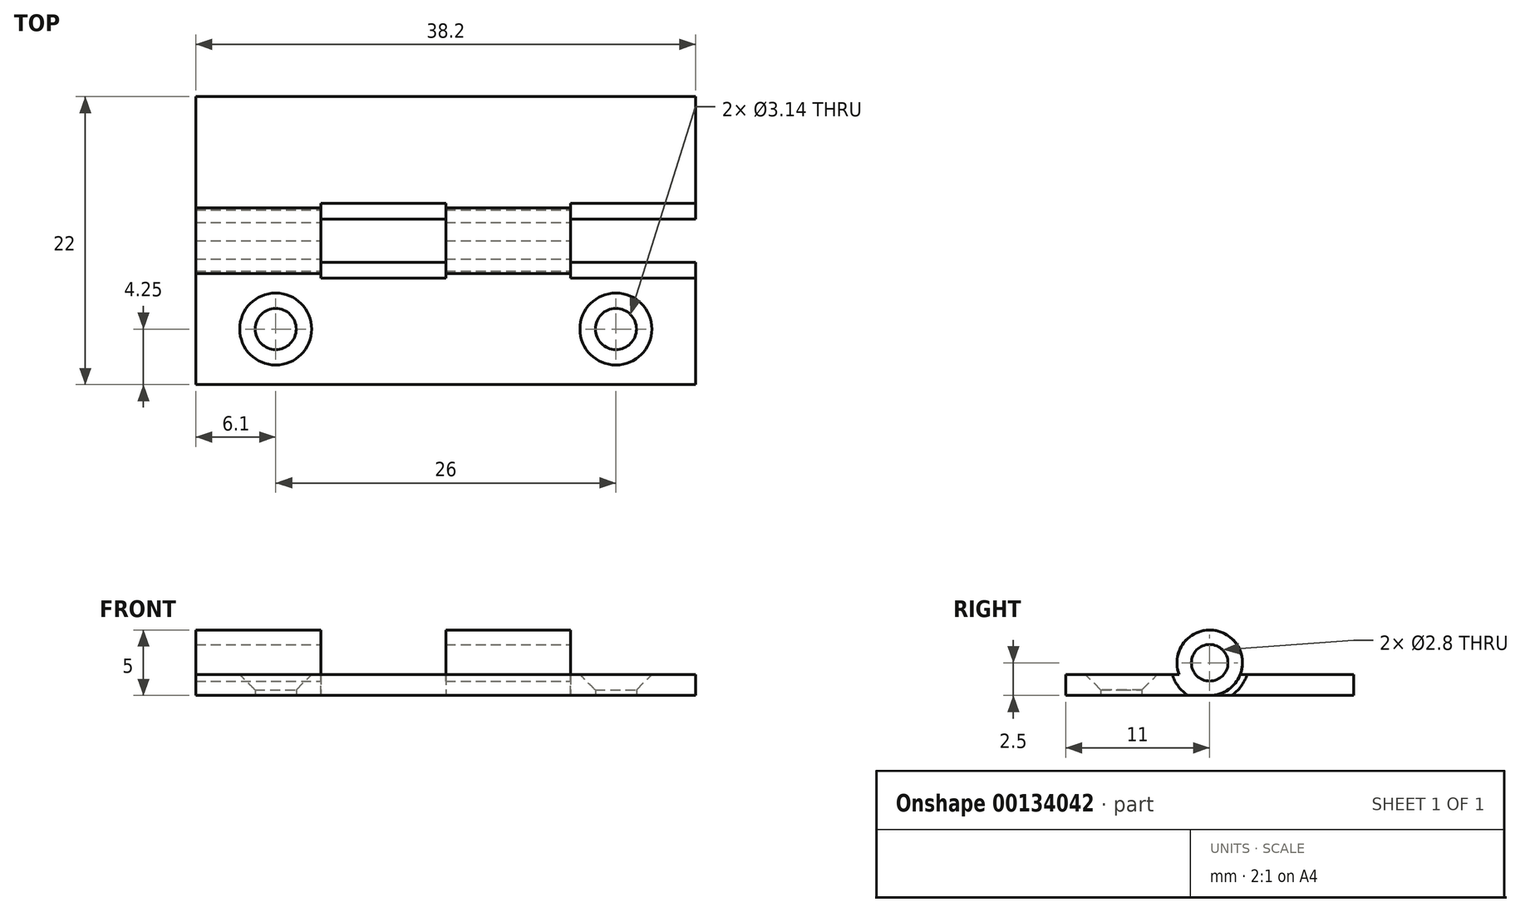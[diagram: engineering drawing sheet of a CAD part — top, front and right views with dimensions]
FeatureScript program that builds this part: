
annotation { "Feature Type Name" : "Feature", "Feature Type Description" : "" }
export const myFeature = defineFeature(function(context is Context, id is Id, definition is map)
    precondition{}
    {
        {
            var Q0;
            Q0=qCreatedBy(makeId("Right.planeOp"),FACE);
            var sketch = newSketch(context, id + "F0", { "sketchPlane" : qUnion([Q0])});
            skCircle(sketch, "E0", {"center": v(0, 0) * mm, "radius": 2.5 * mm});
            skLineSegment(sketch, "E1", {"start": v(0, -2.5) * mm, "end": v(11, -2.5) * mm});
            skLineSegment(sketch, "E2", {"start": v(11, -2.5) * mm, "end": v(11, -0.9) * mm});
            skLineSegment(sketch, "E3", {"start": v(11, -0.9) * mm, "end": v(2.33, -0.9) * mm});
            skLineSegment(sketch, "E4", {"start": v(0, -2.5) * mm, "end": v(0, 0) * mm, "construction": true});
            skLineSegment(sketch, "E5.MirrorCS", {"start": v(-11, -2.5) * mm, "end": v(-11, -0.9) * mm});
            skLineSegment(sketch, "E6.MirrorCS", {"start": v(-11, -0.9) * mm, "end": v(-2.33, -0.9) * mm});
            skLineSegment(sketch, "E7.MirrorCS", {"start": v(0, -2.5) * mm, "end": v(-11, -2.5) * mm});
            skCircle(sketch, "E8", {"center": v(0, 0) * mm, "radius": 1.4 * mm});
            skSolve(sketch);
        }
        {
            var Q0;
            Q0=makeQuery(id+"F0.imprint","IMPRINT",FACE,{"disambiguationData":[TD([[makeQuery(id+"F0.imprint","IMPRINT",EDGE,{"derivedFrom":sQuery(id+"F0.wireOp",EDGE,"E8")}),1.0]])]});
            extrude(context, id + "F1", {"entities" : qUnion([Q0]), "oppositeDirection" : true, "depth" : 38.2 * mm});
        }
        {
            var Q0;
            Q0=makeQuery(id+"F0.imprint","IMPRINT",FACE,{"disambiguationData":[TD([[makeQuery(id+"F0.imprint","IMPRINT",EDGE,{"derivedFrom":sQuery(id+"F0.wireOp",EDGE,"E5.MirrorCS")}),-1.0]])]});
            var Q1;
            Q1=makeQuery(id+"F0.imprint","IMPRINT",FACE,{"disambiguationData":[TD([[makeQuery(id+"F0.imprint","IMPRINT",EDGE,{"derivedFrom":sQuery(id+"F0.wireOp",EDGE,"E8")}),-1.0]])]});
            var Q2;
            Q2=makeQuery(id+"F1.opExtrude","CAP_FACE",FACE,{"disambiguationData":[OSD([sQuery(id+"F0.wireOp",EDGE,"E8")])],"isStart":false});
            extrude(context, id + "F2", {"entities" : qUnion([Q0, Q1]), "endBound" : BoundingType.UP_TO_SURFACE, "oppositeDirection" : true, "endBoundEntityFace" : qUnion([Q2]), "depth" : 38.2 * mm});
        }
        {
            var Q0;
            {var subQ0=sQuery(id+"F0.wireOp",EDGE,"E1");Q0=makeQuery(id+"F0.imprint","IMPRINT",FACE,{"disambiguationData":[TD([[makeQuery(id+"F0.imprint","IMPRINT",EDGE,{"derivedFrom":subQ0}),1.0]])]});}
            var Q1;
            Q1=makeQuery(id+"F0.imprint","IMPRINT",FACE,{"disambiguationData":[TD([[makeQuery(id+"F0.imprint","IMPRINT",EDGE,{"derivedFrom":sQuery(id+"F0.wireOp",EDGE,"E8")}),-1.0]])]});
            var Q2;
            Q2=makeQuery(id+"F1.opExtrude","CAP_FACE",FACE,{"disambiguationData":[OSD([sQuery(id+"F0.wireOp",EDGE,"E8")])],"isStart":false});
            extrude(context, id + "F3", {"entities" : qUnion([Q0, Q1]), "endBound" : BoundingType.UP_TO_SURFACE, "oppositeDirection" : true, "endBoundEntityFace" : qUnion([Q2]), "depth" : 25 * mm});
        }
        {
            var Q0;
            Q0=makeQuery(id+"F2.opExtrude","SWEPT_FACE",FACE,{"disambiguationData":[OSD([sQuery(id+"F0.wireOp",EDGE,"E6.MirrorCS")])]});
            var sketch = newSketch(context, id + "F4", { "sketchPlane" : qUnion([Q0])});
            skPoint(sketch, "E9", {"position": v(-6.1, -6.75) * mm});
            skLineSegment(sketch, "E10", {"start": v(-19.1, -11) * mm, "end": v(-19.1, 0) * mm, "construction": true});
            skPoint(sketch, "E11.MirrorP", {"position": v(-32.1, -6.75) * mm});
            skSolve(sketch);
        }
        {
            var Q0;
            Q0=qCreatedBy(makeId("Top.planeOp"),FACE);
            var sketch = newSketch(context, id + "F5", { "sketchPlane" : qUnion([Q0])});
            skLineSegment(sketch, "E12", {"start": v(0, -2.5) * mm, "end": v(-38.2, -2.5) * mm, "construction": true});
            skLineSegment(sketch, "E13", {"start": v(-38.2, 2.5) * mm, "end": v(0, 2.5) * mm, "construction": true});
            skLineSegment(sketch, "E14", {"start": v(-19.1, -2.5) * mm, "end": v(-19.1, 2.5) * mm, "construction": true});
            skLineSegment(sketch, "E15", {"start": v(-19.1, 0) * mm, "end": v(0, 0) * mm, "construction": true});
            skLineSegment(sketch, "E16", {"start": v(-9.55, 0) * mm, "end": v(-9.55, -3) * mm});
            skLineSegment(sketch, "E17", {"start": v(-9.55, -3) * mm, "end": v(0, -3) * mm});
            skLineSegment(sketch, "E18", {"start": v(0, -3) * mm, "end": v(0, 0) * mm});
            skLineSegment(sketch, "E19", {"start": v(-9.55, 0) * mm, "end": v(0, 0) * mm});
            skLineSegment(sketch, "E20.0", {"start": v(-38.2, 1.4) * mm, "end": v(-38.2, -1.4) * mm, "construction": true});
            skLineSegment(sketch, "E21.1.0.0", {"start": v(-19.1, -3) * mm, "end": v(-19.1, 0) * mm});
            skLineSegment(sketch, "E21.1.0.1", {"start": v(-28.65, -3) * mm, "end": v(-19.1, -3) * mm});
            skLineSegment(sketch, "E21.1.0.2", {"start": v(-28.65, 0) * mm, "end": v(-28.65, -3) * mm});
            skLineSegment(sketch, "E21.1.0.3", {"start": v(-28.65, 0) * mm, "end": v(-19.1, 0) * mm});
            skLineSegment(sketch, "E21.direction1", {"start": v(0, -3) * mm, "end": v(-19.1, -3) * mm, "construction": true});
            skSolve(sketch);
        }
        {
            var Q0;
            Q0=makeQuery(id+"F5.imprint","IMPRINT",FACE,{"disambiguationData":[TD([[makeQuery(id+"F5.imprint","IMPRINT",EDGE,{"derivedFrom":sQuery(id+"F5.wireOp",EDGE,"E16")}),1.0]])]});
            var Q1;
            Q1=makeQuery(id+"F5.imprint","IMPRINT",FACE,{"disambiguationData":[TD([[makeQuery(id+"F5.imprint","IMPRINT",EDGE,{"derivedFrom":sQuery(id+"F5.wireOp",EDGE,"E21.1.0.0")}),1.0]])]});
            var Q2;
            Q2=sQuery(id+"F5.wireOp",EDGE,"E19");
            revolve(context, id + "F6", {"operationType" : NewBodyOperationType.REMOVE, "entities" : qUnion([Q0, Q1]), "axis" : qUnion([Q2]), "revolveType" : RevolveType.FULL, "oppositeDirection" : true});
        }
        {
            var Q0;
            Q0=makeQuery(id+"F2.opExtrude","SWEPT_BODY",BODY,{"disambiguationData":[OSD([sQuery(id+"F0.wireOp",EDGE,"E0"),sQuery(id+"F0.wireOp",EDGE,"E5.MirrorCS"),sQuery(id+"F0.wireOp",EDGE,"E6.MirrorCS"),sQuery(id+"F0.wireOp",EDGE,"E7.MirrorCS"),sQuery(id+"F0.wireOp",EDGE,"E8")])]});
            var Q1;
            Q1=makeQuery(id+"F3.opExtrude","SWEPT_BODY",BODY,{"disambiguationData":[OSD([sQuery(id+"F0.wireOp",EDGE,"E0"),sQuery(id+"F0.wireOp",EDGE,"E1"),sQuery(id+"F0.wireOp",EDGE,"E2"),sQuery(id+"F0.wireOp",EDGE,"E3"),sQuery(id+"F0.wireOp",EDGE,"E8")])]});
            booleanBodies(context, id + "F7", {"operationType" : BooleanOperationType.SUBTRACTION, "tools" : qUnion([Q0]), "targets" : qUnion([Q1]), "keepTools" : true});
        }
        {
            var Q0;
            Q0=sQuery(id+"F4.wireOp",VERTEX,"E11.MirrorP");
            var Q1;
            Q1=sQuery(id+"F4.wireOp",VERTEX,"E9");
            var Q2;
            Q2=sQuery(id+"F6hELVgphqmoUNT_3.1.F4.wireOp",VERTEX,"E9");
            var Q3;
            Q3=sQuery(id+"F6hELVgphqmoUNT_3.1.F4.wireOp",VERTEX,"E11.MirrorP");
            var Q4;
            Q4=makeQuery(id+"F2.opExtrude","SWEPT_BODY",BODY,{"disambiguationData":[OSD([sQuery(id+"F0.wireOp",EDGE,"E0"),sQuery(id+"F0.wireOp",EDGE,"E5.MirrorCS"),sQuery(id+"F0.wireOp",EDGE,"E6.MirrorCS"),sQuery(id+"F0.wireOp",EDGE,"E7.MirrorCS"),sQuery(id+"F0.wireOp",EDGE,"E8")])]});
            var Q5;
            Q5=makeQuery(id+"F3.opExtrude","SWEPT_BODY",BODY,{"disambiguationData":[OSD([sQuery(id+"F0.wireOp",EDGE,"E0"),sQuery(id+"F0.wireOp",EDGE,"E1"),sQuery(id+"F0.wireOp",EDGE,"E2"),sQuery(id+"F0.wireOp",EDGE,"E3"),sQuery(id+"F0.wireOp",EDGE,"E8")])]});
            hole(context, id + "F8", {"style" : HoleStyle.C_SINK, "endStyle" : HoleEndStyle.THROUGH, "holeDiameter" : 3.14 * mm, "cSinkDiameter" : 5.5 * mm, "cSinkAngle" : 90 * degree, "locations" : qUnion([Q0, Q1, Q2, Q3]), "scope" : qUnion([Q4, Q5]), "isTappedThrough" : true, "startStyle" : HoleStartStyle.PART});
        }
    });
